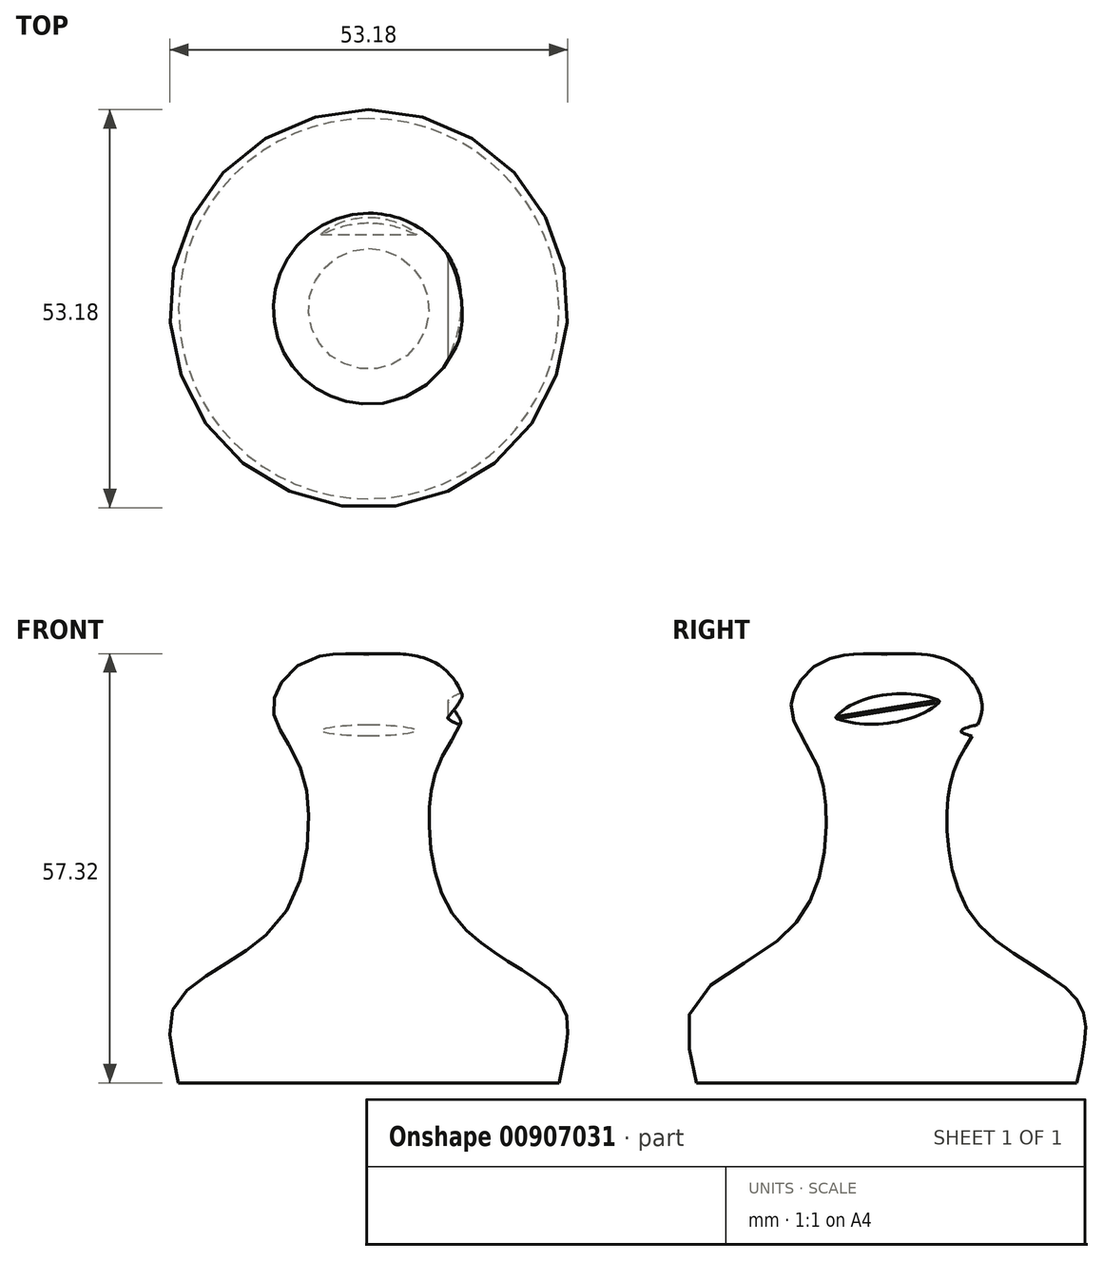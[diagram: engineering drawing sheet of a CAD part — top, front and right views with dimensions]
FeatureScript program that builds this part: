
annotation { "Feature Type Name" : "Feature", "Feature Type Description" : "" }
export const myFeature = defineFeature(function(context is Context, id is Id, definition is map)
    precondition{}
    {
        {
            var Q0;
            Q0=qCreatedBy(makeId("Right.planeOp"),FACE);
            var sketch = newSketch(context, id + "F0", { "sketchPlane" : qUnion([Q0])});
            skLineSegment(sketch, "E0", {"start": v(0, 0) * mm, "end": v(25.4, 0) * mm});
            skFitSpline(sketch, "E1", {"points": [v(25.4, 0) * mm, v(25.4, 11.14) * mm, v(12.15, 21.33) * mm, v(8.07, 36) * mm, v(9.7, 43.35) * mm, v(12.7, 49.46) * mm, v(11.33, 53.95) * mm, v(7.25, 56.8) * mm, v(0, 57.15) * mm], "startDerivative": vector(22.91, 106) * mm, "endDerivative": vector(-62.8, -6.52) * mm});
            skLineSegment(sketch, "E2", {"start": v(0, 57.15) * mm, "end": v(0, 0) * mm});
            skSolve(sketch);
        }
        {
            var Q0;
            Q0=makeQuery(id+"F0.imprint","IMPRINT",FACE,{"disambiguationData":[TD([[makeQuery(id+"F0.imprint","IMPRINT",EDGE,{"derivedFrom":sQuery(id+"F0.wireOp",EDGE,"E0")}),1.0]])]});
            var Q1;
            Q1=sQuery(id+"F0.wireOp",EDGE,"E2");
            revolve(context, id + "F1", {"surfaceOperationType" : NewSurfaceOperationType.NEW, "entities" : qUnion([Q0]), "axis" : qUnion([Q1]), "revolveType" : RevolveType.FULL});
        }
        {
            var Q0;
            Q0=qCreatedBy(makeId("Right.planeOp"),FACE);
            cPlane(context, id + "F2", {"entities" : qUnion([Q0]), "cplaneType" : CPlaneType.OFFSET, "offset" : 12.7 * mm, "width" : 152.4 * mm, "height" : 152.4 * mm});
        }
        {
            var Q0;
            Q0=qCreatedBy(id+"F2.planeOp",FACE);
            var sketch = newSketch(context, id + "F3", { "sketchPlane" : qUnion([Q0])});
            skLineSegment(sketch, "E3", {"start": v(0, 54.65) * mm, "end": v(0, 27.18) * mm, "construction": true});
            skLineSegment(sketch, "E4", {"start": v(-13.57, 47) * mm, "end": v(12.44, 47) * mm, "construction": true});
            skLineSegment(sketch, "E5", {"start": v(12.44, 47.94) * mm, "end": v(12.44, 46.04) * mm});
            skFitSpline(sketch, "E6", {"points": [v(12.44, 46.04) * mm, v(9.9, 47) * mm, v(12.44, 47.94) * mm], "startDerivative": vector(-6.24, 1.9) * mm, "endDerivative": vector(6.24, 1.9) * mm});
            skSolve(sketch);
        }
        {
            var Q0;
            Q0=makeQuery(id+"F3.imprint","IMPRINT",FACE,{"disambiguationData":[TD([[makeQuery(id+"F3.imprint","IMPRINT",EDGE,{"derivedFrom":sQuery(id+"F3.wireOp",EDGE,"E5")}),-1.0]])]});
            extrude(context, id + "F4", {"entities" : qUnion([Q0]), "operationType" : NewBodyOperationType.REMOVE, "oppositeDirection" : true, "depth" : 25.4 * mm, "offsetDistance" : 25.4 * mm});
        }
        {
            var Q0;
            Q0=qCreatedBy(makeId("Front.planeOp"),FACE);
            cPlane(context, id + "F5", {"entities" : qUnion([Q0]), "cplaneType" : CPlaneType.OFFSET, "offset" : 25.4 * mm, "width" : 152.4 * mm, "height" : 152.4 * mm});
        }
        {
            var Q0;
            Q0=qCreatedBy(makeId("Front.planeOp"),FACE);
            cPlane(context, id + "F6", {"entities" : qUnion([Q0]), "cplaneType" : CPlaneType.OFFSET, "offset" : 25.4 * mm, "oppositeDirection" : true, "width" : 152.4 * mm, "height" : 152.4 * mm});
        }
        {
            var Q0;
            Q0=qCreatedBy(id+"F5.planeOp",FACE);
            var sketch = newSketch(context, id + "F7", { "sketchPlane" : qUnion([Q0])});
            skLineSegment(sketch, "E7.bottom", {"start": v(14.95, 45.72) * mm, "end": v(12.7, 43.47) * mm});
            skLineSegment(sketch, "E7.top", {"start": v(12.7, 47.97) * mm, "end": v(10.63, 45.9) * mm});
            skLineSegment(sketch, "E7.left", {"start": v(14.95, 45.72) * mm, "end": v(12.7, 47.97) * mm});
            skLineSegment(sketch, "E7.right", {"start": v(12.7, 43.47) * mm, "end": v(10.63, 45.54) * mm});
            skPoint(sketch, "E7.middle", {"position": v(12.7, 45.72) * mm});
            skLineSegment(sketch, "E8", {"start": v(12.7, 43.47) * mm, "end": v(23.82, 43.47) * mm, "construction": true});
            skPoint(sketch, "E9.visualSharp", {"position": v(10.45, 45.72) * mm});
            skArc(sketch, "E9.filletArc", {"start": v(10.63, 45.9) * mm, "mid": v(10.56, 45.72) * mm, "end": v(10.63, 45.54) * mm});
            skSolve(sketch);
        }
        {
            var Q0;
            Q0=qCreatedBy(id+"F6.planeOp",FACE);
            var sketch = newSketch(context, id + "F8", { "sketchPlane" : qUnion([Q0])});
            skLineSegment(sketch, "E10.bottom", {"start": v(14.95, 53.98) * mm, "end": v(12.7, 51.73) * mm});
            skLineSegment(sketch, "E10.top", {"start": v(12.7, 56.22) * mm, "end": v(10.63, 54.15) * mm});
            skLineSegment(sketch, "E10.left", {"start": v(14.95, 53.98) * mm, "end": v(12.7, 56.22) * mm});
            skLineSegment(sketch, "E10.right", {"start": v(12.7, 51.73) * mm, "end": v(10.63, 53.8) * mm});
            skPoint(sketch, "E10.middle", {"position": v(12.7, 53.97) * mm});
            skLineSegment(sketch, "E11", {"start": v(12.7, 51.73) * mm, "end": v(20.63, 51.73) * mm, "construction": true});
            skPoint(sketch, "E12.visualSharp", {"position": v(10.45, 53.97) * mm});
            skArc(sketch, "E12.filletArc", {"start": v(10.63, 54.15) * mm, "mid": v(10.56, 53.97) * mm, "end": v(10.63, 53.8) * mm});
            skSolve(sketch);
        }
        {
            var Q1;
            Q1=makeQuery(id+"F7.imprint","IMPRINT",FACE,{"disambiguationData":[TD([[makeQuery(id+"F7.imprint","IMPRINT",EDGE,{"derivedFrom":sQuery(id+"F7.wireOp",EDGE,"E7.bottom")}),-1.0]])]});
            var Q2;
            Q2=makeQuery(id+"F8.imprint","IMPRINT",FACE,{"disambiguationData":[TD([[makeQuery(id+"F8.imprint","IMPRINT",EDGE,{"derivedFrom":sQuery(id+"F8.wireOp",EDGE,"E10.bottom")}),-1.0]])]});
            loft(context, id + "F9", {"operationType" : NewBodyOperationType.REMOVE, "sheetProfilesArray" : [{ "sheetProfileEntities" : qUnion([Q1]) }, { "sheetProfileEntities" : qUnion([Q2]) }]});
        }
    });
